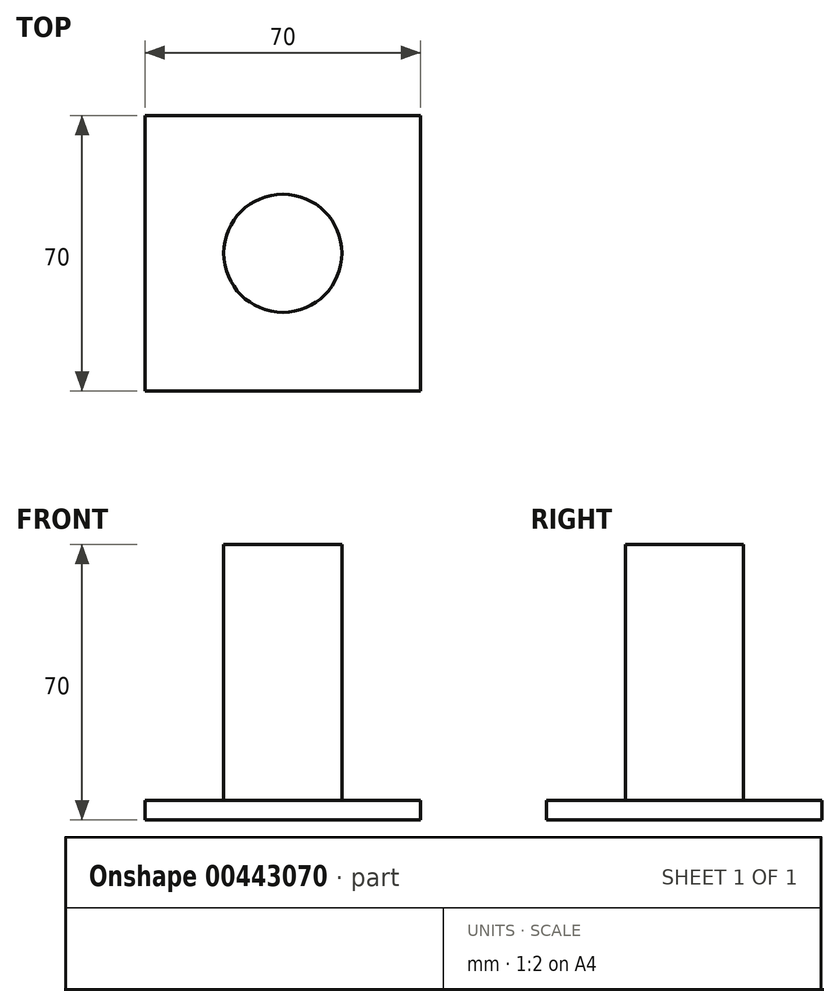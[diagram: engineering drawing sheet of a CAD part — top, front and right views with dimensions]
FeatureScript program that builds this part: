
annotation { "Feature Type Name" : "Feature", "Feature Type Description" : "" }
export const myFeature = defineFeature(function(context is Context, id is Id, definition is map)
    precondition{}
    {
        {
            var Q0;
            Q0=qCreatedBy(makeId("Top.planeOp"),FACE);
            var sketch = newSketch(context, id + "F0", { "sketchPlane" : qUnion([Q0])});
            skLineSegment(sketch, "E0.bottom", {"start": v(-41.3, -27.65) * mm, "end": v(28.7, -27.65) * mm});
            skLineSegment(sketch, "E0.top", {"start": v(-41.3, 42.35) * mm, "end": v(28.7, 42.35) * mm});
            skLineSegment(sketch, "E0.left", {"start": v(-41.3, -27.65) * mm, "end": v(-41.3, 42.35) * mm});
            skLineSegment(sketch, "E0.right", {"start": v(28.7, -27.65) * mm, "end": v(28.7, 42.35) * mm});
            skPoint(sketch, "E1", {"position": v(-6.3, -27.65) * mm});
            skLineSegment(sketch, "E2", {"start": v(-6.3, -27.65) * mm, "end": v(-6.3, 7.35) * mm});
            skCircle(sketch, "E3", {"center": v(-6.3, 7.35) * mm, "radius": 15 * mm});
            skSolve(sketch);
        }
        {
            var Q0;
            Q0 = qSketchRegion(id + "F0", true);
            extrude(context, id + "F1", {"entities" : qUnion([Q0]), "depth" : 5 * mm});
        }
        {
            var Q0;
            Q0=makeQuery(id+"F0.imprint","IMPRINT",FACE,{"disambiguationData":[TD([[makeQuery(id+"F0.imprint","IMPRINT",EDGE,{"derivedFrom":sQuery(id+"F0.wireOp",EDGE,"E3")}),1.0]])]});
            extrude(context, id + "F2", {"entities" : qUnion([Q0]), "operationType" : NewBodyOperationType.ADD, "depth" : 70 * mm});
        }
    });
